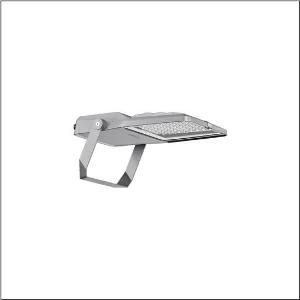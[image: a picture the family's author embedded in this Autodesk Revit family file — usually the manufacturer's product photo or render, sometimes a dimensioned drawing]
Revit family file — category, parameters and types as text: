
# Revit family: floodlight_fl_21_iq_mini___pl64_5xa7772d5e1a_506a
name_source: partatom
category: Lighting Fixtures
units: mm (PartAtom-declared; Revit-internal decimal feet)

## family parameters
Cut with Voids When Loaded = No
Host = Face
Light Source = No
Part Type = Normal
Room Calculation Point = No
Round Connector Dimension = Use Diameter
Shared = No

## types (1)
- --- (1 x LED, 16070 lm, 143 W, 4000K)
    Apparent Load = 143 VA
    CIE Flux Codes = 28 80 98 100 100
    Color Rendering = 80
    Color Temperature = 4000K
    Default Elevation = 1800 mm
    Description = Floodlight FL 21 iQ mini, floodlight, primary light control with lens, of PMMA, primary optical cover: protective disc, of toughened safety glass, transparent, light distribution: PL64, light emission: direct distribution, installation type: surface-mounted, LED, High Power LED, rated luminous flux: 16.070lm, luminous efficacy: 112lm/W, light colour: 840, colour temperature: 4000K, control: Street-Remote, Auto-Match, Temp-Guard, Night-Set, Smart-Wire, Desk-Remote (wireless, voltage-free reading and setting of iQ features in the workshop via application-optimized NFC function/RFID function), optimised constant luminous flux control (CLO 2.0), with terminal, 6-pole, mains connection: 220..240V, AC, 50/60Hz, start of lifetime: 143W, end of service life: 152W, reduction: 61W, luminaire housing, of diecast aluminium, powder-coated, Siteco® metallic grey (DB 702S), corrosivity category C5 mid according to DIN EN ISO 12944, sealing non-destructively replaceable, mounting bracket, of steel, galvanised, powder-coated, Siteco® metallic grey (DB 702S), protection rating (complete): IP66, insulation class (complete): insulation class II (safety insulation), certification: CE, ENEC, VDE, protection symbol: D, impact resistance: IK08, permissible operating ambient temperature: -40..+40°C, permissible operating ambient temperature for outdoor applications: -40..+50°C, standard: DIN EN 12944, LABS conformity tested according to VDMA 24364:2018-05, packaging unit: 1 piece

Light Distribution: PL64
    Height = 70 mm
    Lamp = 1 x LED
    Lamp Light Flux = 16070 lm
    Lamp Power = 143 W
    Lamp count = 1
    Length = 485 mm
    Luminous efficacy = 112 lm/W
    Manufacturer = Siteco
    ModVariant = No
    Model = 5XA7772D5E1A
    Number of Poles = 1
    OnlyDefault = Yes
    Power Factor = 1
    Product Name = Floodlight FL 21 iQ mini | PL64
    Product group = floodlight | pylon annexe
    ProductGroupID = 6200
    Protection Class = Protection class II
    Protection Degree = IP 66
    RLX_Detail_Level = 1
    RLX_Emergency_Light_Flux = 0 lm
    RLX_Emergency_Type = 0
    RLX_Emergency_Type_DB = No
    RlxData = <blob elided: 96533 chars, md5=f170b487>
    Socket = socket
    Standby Power = 0 W
    System Light Flux = 16070 lm
    System Power = 143 W
    Type Comments = factory setting: luminous flux: 100 % | dim-lin: 254 | 730 mA
    Type Image = l_1006845.jpg
    URL = http://relux.com
    VarID = @adj_115763
    Voltage = 0 V
    Weight = 0.00 kg
    Width = 337 mm

## geometry (parser evidence)
native form markers: Blend x4, Sweep x12
no freeform markers — native parametric forms only
